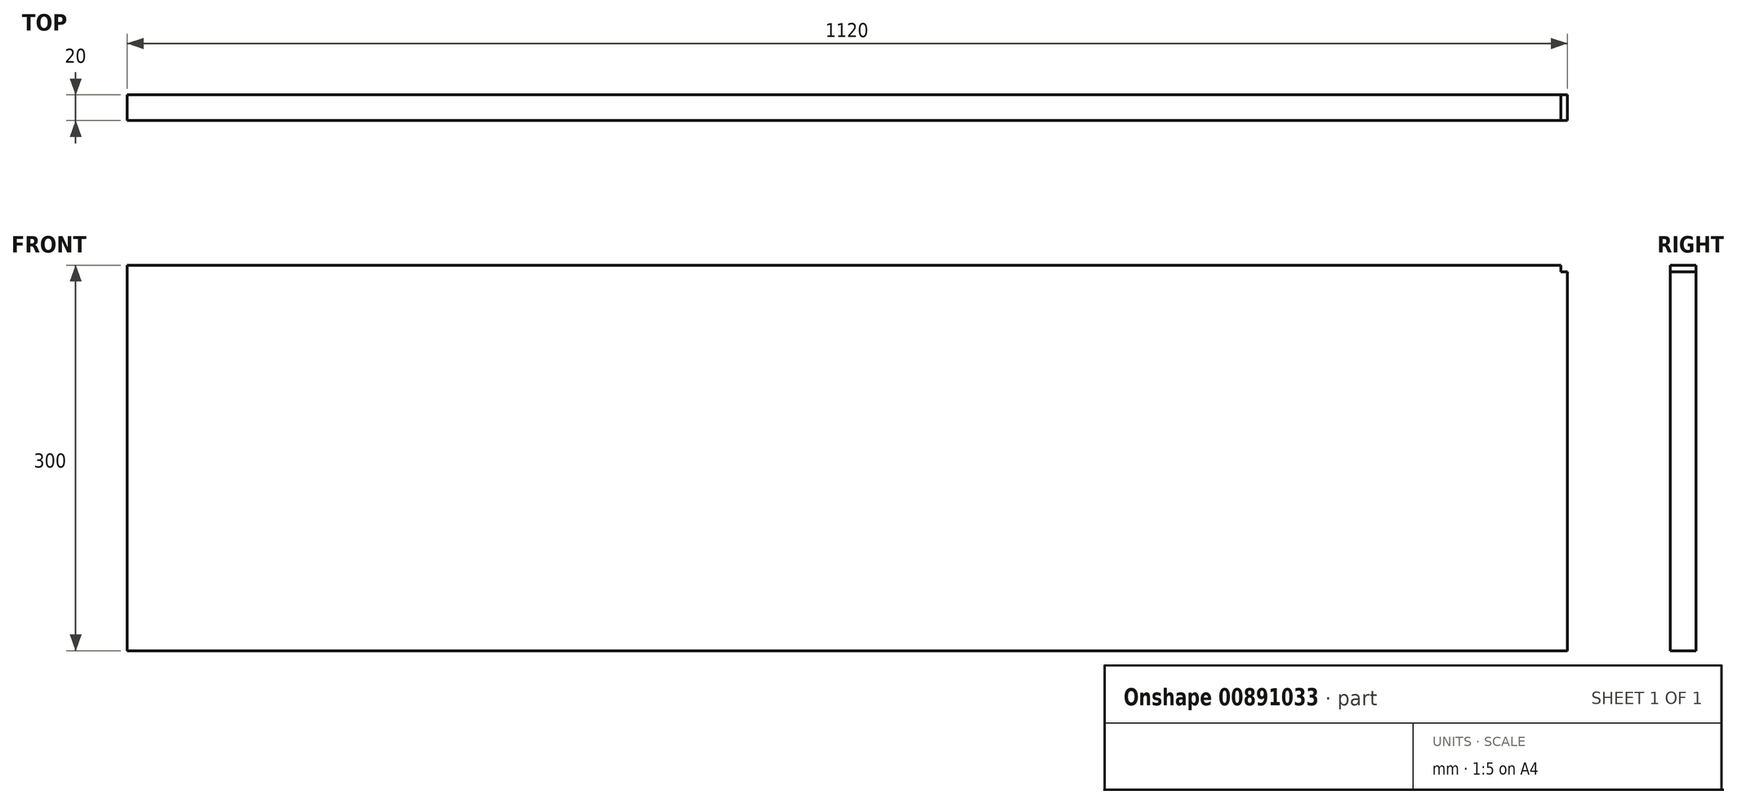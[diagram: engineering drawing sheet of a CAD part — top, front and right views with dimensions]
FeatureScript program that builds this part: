
annotation { "Feature Type Name" : "Feature", "Feature Type Description" : "" }
export const myFeature = defineFeature(function(context is Context, id is Id, definition is map)
    precondition{}
    {
        {
            var Q0;
            Q0=qCreatedBy(makeId("Front.planeOp"),FACE);
            var sketch = newSketch(context, id + "F0", { "sketchPlane" : qUnion([Q0])});
            skLineSegment(sketch, "E0.bottom", {"start": v(560, -150) * mm, "end": v(-560, -150) * mm});
            skLineSegment(sketch, "E0.top", {"start": v(560, 150) * mm, "end": v(-560, 150) * mm});
            skLineSegment(sketch, "E0.left", {"start": v(560, -150) * mm, "end": v(560, 150) * mm});
            skLineSegment(sketch, "E0.right", {"start": v(-560, -150) * mm, "end": v(-560, 150) * mm});
            skPoint(sketch, "E0.middle", {"position": v(0, 0) * mm});
            skLineSegment(sketch, "E1.bottom", {"start": v(560, 150) * mm, "end": v(555, 150) * mm});
            skLineSegment(sketch, "E1.top", {"start": v(560, 145) * mm, "end": v(555, 145) * mm});
            skLineSegment(sketch, "E1.left", {"start": v(560, 150) * mm, "end": v(560, 145) * mm});
            skLineSegment(sketch, "E1.right", {"start": v(555, 150) * mm, "end": v(555, 145) * mm});
            skSolve(sketch);
        }
        {
            var Q0;
            Q0=makeQuery(id+"F0.imprint","IMPRINT",FACE,{"disambiguationData":[TD([[makeQuery(id+"F0.imprint","IMPRINT",EDGE,{"derivedFrom":sQuery(id+"F0.wireOp",EDGE,"E0.bottom")}),-1.0]])]});
            extrude(context, id + "F1", {"entities" : qUnion([Q0]), "depth" : 20 * mm, "offsetDistance" : 25 * mm});
        }
    });
